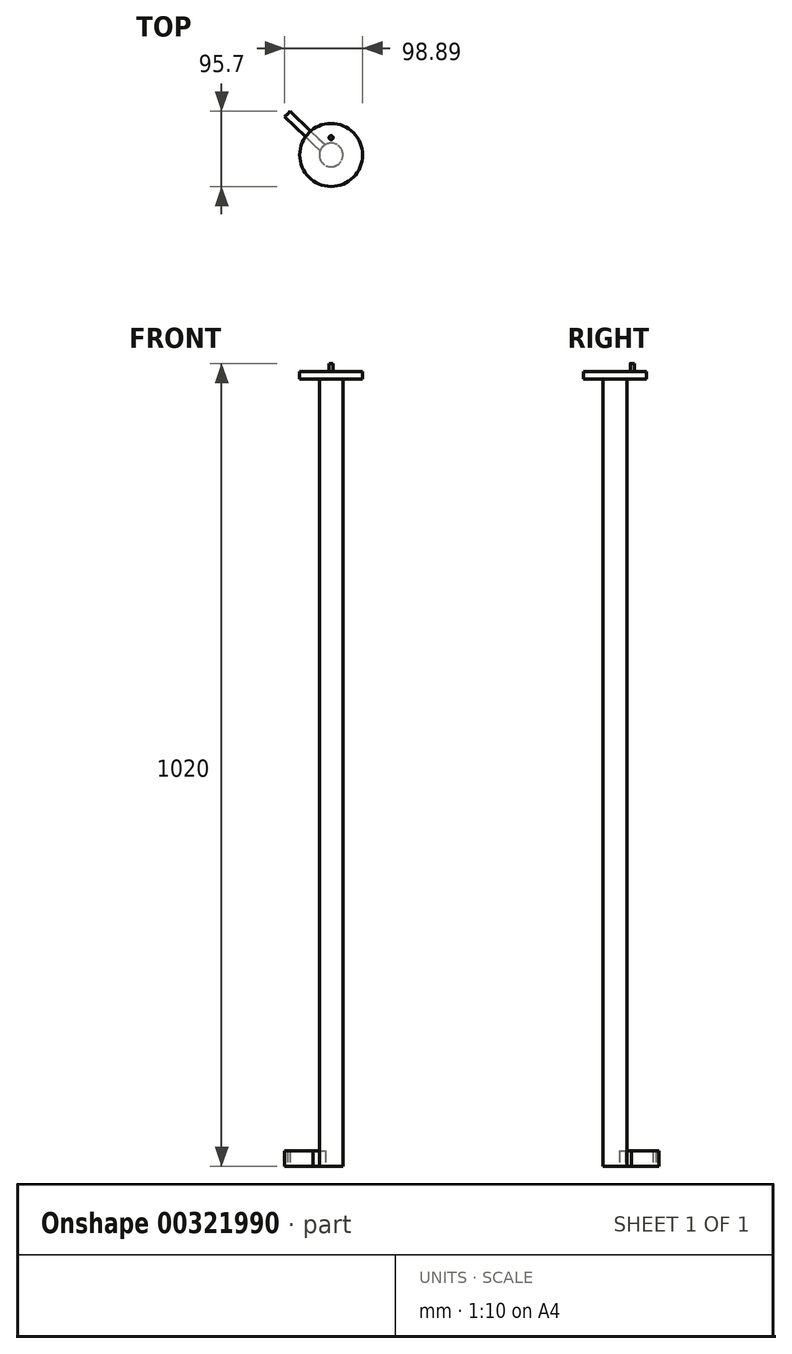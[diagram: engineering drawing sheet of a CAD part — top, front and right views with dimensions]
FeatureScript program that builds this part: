
annotation { "Feature Type Name" : "Feature", "Feature Type Description" : "" }
export const myFeature = defineFeature(function(context is Context, id is Id, definition is map)
    precondition{}
    {
        {
            var Q0;
            Q0=qCreatedBy(makeId("Top.planeOp"),FACE);
            var sketch = newSketch(context, id + "F0", { "sketchPlane" : qUnion([Q0])});
            skCircle(sketch, "E0", {"center": v(0, 0) * mm, "radius": 40 * mm});
            skSolve(sketch);
        }
        {
            var Q0;
            Q0 = qSketchRegion(id + "F0", true);
            extrude(context, id + "F1", {"entities" : qUnion([Q0]), "depth" : 10 * mm});
        }
        {
            var Q0;
            Q0=makeQuery(id+"F1.opExtrude","CAP_FACE",FACE,{"disambiguationData":[OSD([sQuery(id+"F0.wireOp",EDGE,"E0")])],"isStart":false});
            var sketch = newSketch(context, id + "F2", { "sketchPlane" : qUnion([Q0])});
            skLineSegment(sketch, "E1", {"start": v(0, 0) * mm, "end": v(0, 22) * mm, "construction": true});
            skCircle(sketch, "E2", {"center": v(0, 22) * mm, "radius": 2.5 * mm});
            skSolve(sketch);
        }
        {
            var Q0;
            Q0 = qSketchRegion(id + "F2", true);
            extrude(context, id + "F3", {"entities" : qUnion([Q0]), "operationType" : NewBodyOperationType.ADD, "depth" : 10 * mm});
        }
        {
            var Q0;
            Q0=makeQuery(id+"F1.opExtrude","CAP_FACE",FACE,{"disambiguationData":[OSD([sQuery(id+"F0.wireOp",EDGE,"E0")])],"isStart":true});
            var sketch = newSketch(context, id + "F4", { "sketchPlane" : qUnion([Q0])});
            skCircle(sketch, "E3", {"center": v(0, 0) * mm, "radius": 15 * mm});
            skSolve(sketch);
        }
        {
            var Q0;
            Q0 = qSketchRegion(id + "F4", true);
            extrude(context, id + "F5", {"entities" : qUnion([Q0]), "operationType" : NewBodyOperationType.ADD, "depth" : 1000 * mm});
        }
        {
            var Q0;
            Q0=makeQuery(id+"F5.opExtrude","CAP_FACE",FACE,{"disambiguationData":[OSD([sQuery(id+"F4.wireOp",EDGE,"E3")])],"isStart":false});
            var sketch = newSketch(context, id + "F6", { "sketchPlane" : qUnion([Q0])});
            skLineSegment(sketch, "E4", {"start": v(0, 0) * mm, "end": v(9.99, -11.19) * mm});
            skLineSegment(sketch, "E5", {"start": v(9.99, -11.19) * mm, "end": v(0, 0) * mm});
            skLineSegment(sketch, "E6", {"start": v(0, 0) * mm, "end": v(-19.38, -17.3) * mm});
            skLineSegment(sketch, "E7", {"start": v(-19.38, -17.3) * mm, "end": v(-16.05, -21.04) * mm});
            skLineSegment(sketch, "E8", {"start": v(-16.05, -21.04) * mm, "end": v(3.33, -3.73) * mm});
            skLineSegment(sketch, "E9", {"start": v(0, 0) * mm, "end": v(-9.99, 11.19) * mm});
            skLineSegment(sketch, "E10", {"start": v(-3.24, 3.8) * mm, "end": v(-22.85, -13.7) * mm});
            skLineSegment(sketch, "E11", {"start": v(-22.85, -13.7) * mm, "end": v(-19.38, -17.3) * mm});
            skSolve(sketch);
        }
        {
            var Q0;
            {var subQ0=sQuery(id+"F6.wireOp",EDGE,"E7");Q0=makeQuery(id+"F6.imprint","IMPRINT",FACE,{"disambiguationData":[TD([[makeQuery(id+"F6.imprint","IMPRINT",EDGE,{"derivedFrom":subQ0}),1.0]])]});}
            var Q1;
            {var subQ0=sQuery(id+"F6.wireOp",EDGE,"E11");Q1=makeQuery(id+"F6.imprint","IMPRINT",FACE,{"disambiguationData":[TD([[makeQuery(id+"F6.imprint","IMPRINT",EDGE,{"derivedFrom":subQ0}),1.0]])]});}
            extrude(context, id + "F7", {"entities" : qUnion([Q0, Q1]), "operationType" : NewBodyOperationType.ADD, "oppositeDirection" : true, "depth" : 20 * mm});
        }
        {
            var Q0;
            Q0=makeQuery(id+"F7.opExtrude","SWEPT_FACE",FACE,{"disambiguationData":[OSD([sQuery(id+"F6.wireOp",EDGE,"E11")])]});
            var Q1;
            Q1=makeQuery(id+"F7.opExtrude","SWEPT_FACE",FACE,{"disambiguationData":[OSD([sQuery(id+"F6.wireOp",EDGE,"E7")])]});
            extrude(context, id + "F8", {"entities" : qUnion([Q0, Q1]), "operationType" : NewBodyOperationType.ADD, "depth" : 50 * mm});
        }
    });
